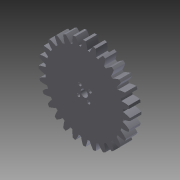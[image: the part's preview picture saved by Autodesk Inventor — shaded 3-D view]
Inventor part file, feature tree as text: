
AUTODESK INVENTOR PART (.ipt)
format: ipt  version: 2015 (Build 190159000, 159)  size: 242,688 bytes
history: native  units: mm (DEFAULTED — no unit token found)
features: plane x3, other x3, sketch x3, extrude x2
ambient origin geometry x8: Origin, YZ Plane, XZ Plane, XY Plane, X Axis, Y Axis, Z Axis, Center Point
bodies: Solid1 (feature_tree)
feature tree (11):
  extrude  "Extrusion1"  Depth=12.7mm TaperAngle=0.0deg
  plane  "Work Plane1"
  plane  "Work Plane2"
  plane  "Work Plane3"
  other  "Spur Gear"
  extrude  "Extrusion2"  Depth=76.2mm TaperAngle=0.0deg
  sketch  "Sketch1"  dims[d0=101.6mm d1=12.7mm d2=0.0mm]
  sketch  "Sketch2"  dims[d3=94.826667mm d4=76.2mm d5=0.0mm]
  other  "Srf1"
  sketch  "Sketch3"  dims[d6=0.0mm d7=1.121997mm d9=0.0mm d14=0.0mm d15=96.52mm d16=0.0mm d17=0.0mm d18=0.0mm d19=96.52mm d20=25.4mm d21=0.0mm]
  other  "Pitch Diameter"
